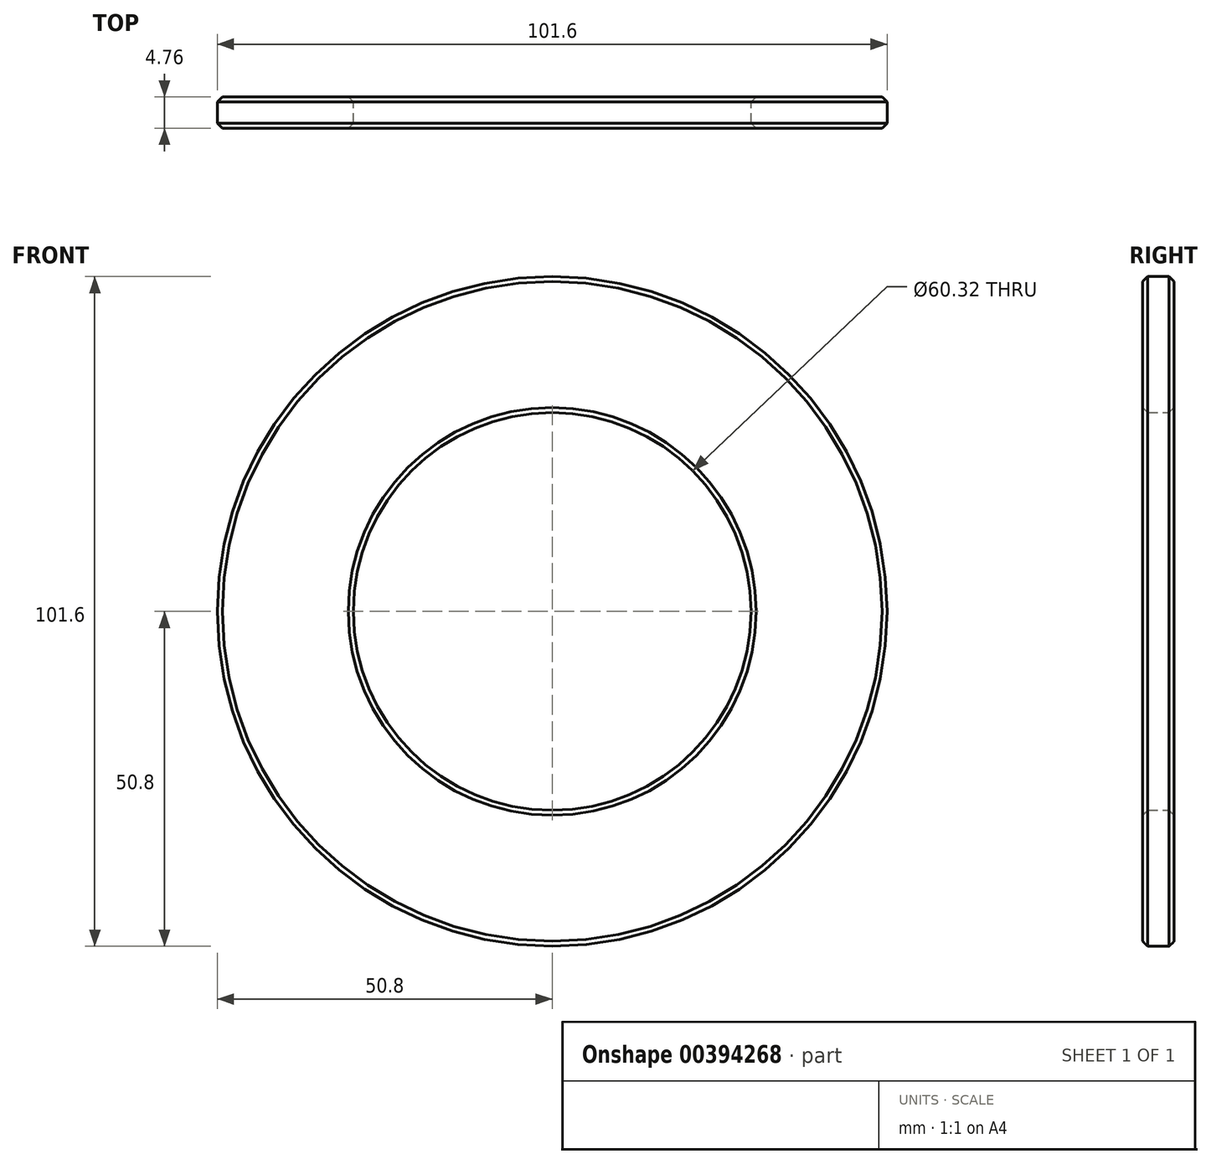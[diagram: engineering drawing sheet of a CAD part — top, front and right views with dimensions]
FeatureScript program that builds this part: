
annotation { "Feature Type Name" : "Feature", "Feature Type Description" : "" }
export const myFeature = defineFeature(function(context is Context, id is Id, definition is map)
    precondition{}
    {
        {
            var Q0;
            Q0=qCreatedBy(makeId("Front.planeOp"),FACE);
            var sketch = newSketch(context, id + "F0", { "sketchPlane" : qUnion([Q0])});
            skCircle(sketch, "E0", {"center": v(0, 0) * mm, "radius": 50.8 * mm});
            skCircle(sketch, "E1", {"center": v(0, 0) * mm, "radius": 30.16 * mm});
            skSolve(sketch);
        }
        {
            var Q0;
            Q0=makeQuery(id+"F0.imprint","IMPRINT",FACE,{"disambiguationData":[TD([[makeQuery(id+"F0.imprint","IMPRINT",EDGE,{"derivedFrom":sQuery(id+"F0.wireOp",EDGE,"E0")}),1.0]])]});
            extrude(context, id + "F1", {"entities" : qUnion([Q0]), "depth" : 4.76 * mm});
        }
        {
            var Q0;
            Q0=makeQuery(id+"F1.opExtrude","CAP_EDGE",EDGE,{"disambiguationData":[OSD([sQuery(id+"F0.wireOp",EDGE,"E0")])],"isStart":true});
            var Q1;
            Q1=makeQuery(id+"F1.opExtrude","CAP_EDGE",EDGE,{"disambiguationData":[OSD([sQuery(id+"F0.wireOp",EDGE,"E0")])],"isStart":false});
            var Q2;
            Q2=makeQuery(id+"F1.opExtrude","CAP_EDGE",EDGE,{"disambiguationData":[OSD([sQuery(id+"F0.wireOp",EDGE,"E1")])],"isStart":true});
            var Q3;
            Q3=makeQuery(id+"F1.opExtrude","CAP_EDGE",EDGE,{"disambiguationData":[OSD([sQuery(id+"F0.wireOp",EDGE,"E1")])],"isStart":false});
            chamfer(context, id + "F2", {"entities" : qUnion([Q0, Q1, Q2, Q3]), "width" : 0.76 * mm, "tangentPropagation" : true});
        }
    });
